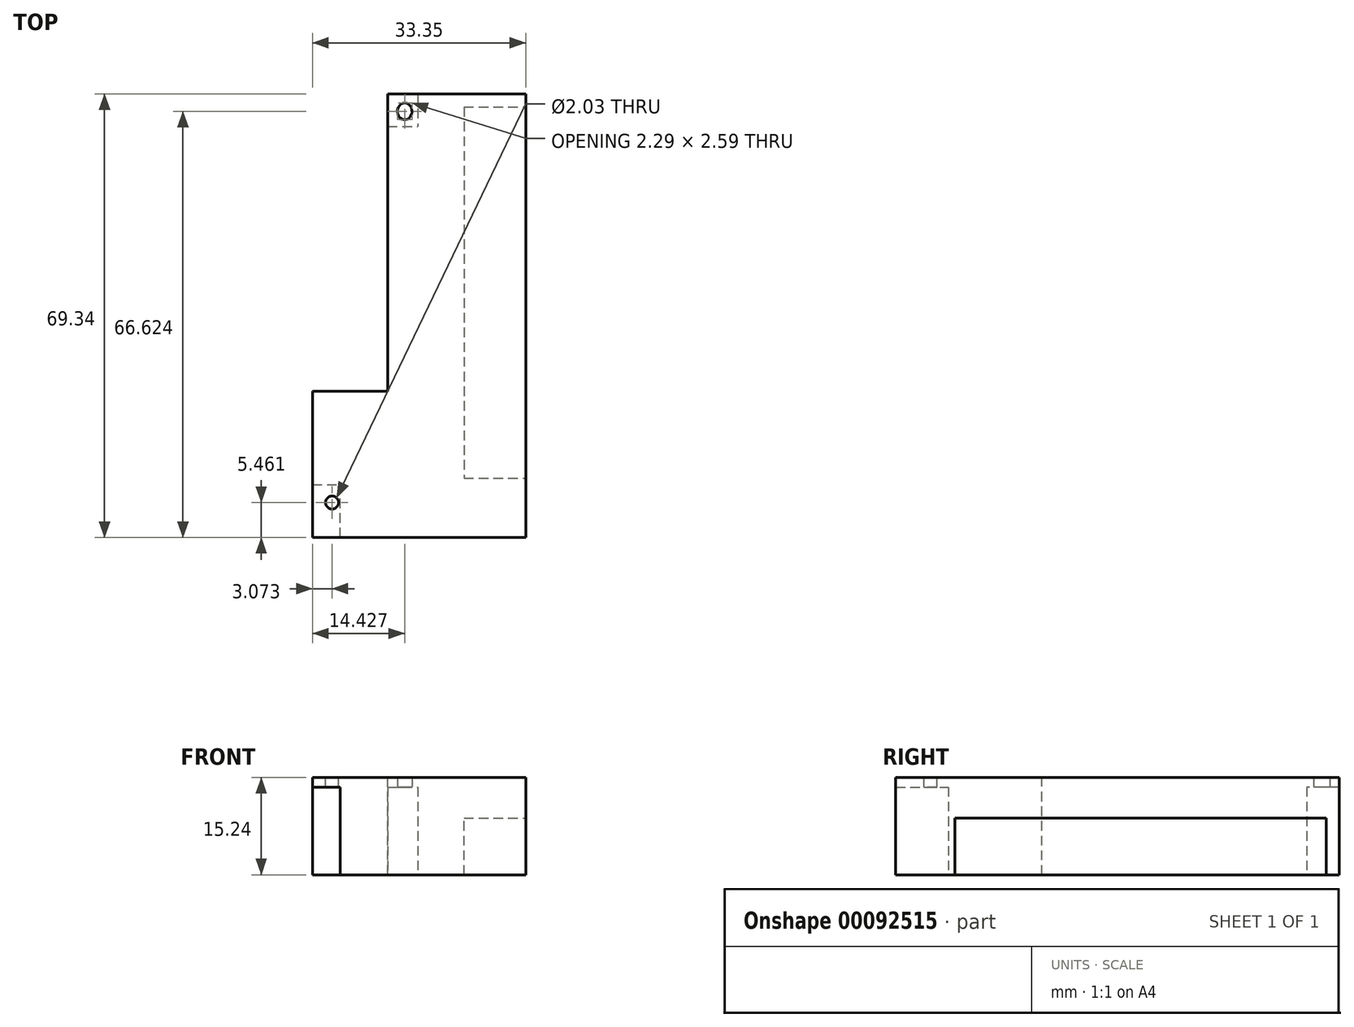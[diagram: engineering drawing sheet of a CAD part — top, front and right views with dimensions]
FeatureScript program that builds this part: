
annotation { "Feature Type Name" : "Feature", "Feature Type Description" : "" }
export const myFeature = defineFeature(function(context is Context, id is Id, definition is map)
    precondition{}
    {
        {
            var Q0;
            Q0=qCreatedBy(makeId("Top.planeOp"),FACE);
            var sketch = newSketch(context, id + "F0", { "sketchPlane" : qUnion([Q0])});
            skLineSegment(sketch, "E0.bottom", {"start": v(-21.6, 69.34) * mm, "end": v(0, 69.34) * mm});
            skLineSegment(sketch, "E0.top", {"start": v(-21.6, 0) * mm, "end": v(0, 0) * mm});
            skLineSegment(sketch, "E0.left", {"start": v(-21.6, 69.34) * mm, "end": v(-21.6, 22.86) * mm});
            skLineSegment(sketch, "E0.right", {"start": v(0, 69.34) * mm, "end": v(0, 0) * mm});
            skLineSegment(sketch, "E1.bottom", {"start": v(-21.6, 0) * mm, "end": v(-33.35, 0) * mm});
            skLineSegment(sketch, "E1.top", {"start": v(-21.6, 22.86) * mm, "end": v(-33.35, 22.86) * mm});
            skLineSegment(sketch, "E1.right", {"start": v(-33.35, 0) * mm, "end": v(-33.35, 22.86) * mm});
            skCircle(sketch, "E2", {"center": v(-30.28, 5.46) * mm, "radius": 1.02 * mm});
            skLineSegment(sketch, "E3", {"start": v(-33.35, 9.14) * mm, "end": v(0, 9.14) * mm});
            skEllipse(sketch, "E4", {"center": v(-18.92, 66.62) * mm, "majorRadius": 1.3 * mm, "minorRadius": 1.14 * mm, "majorAxis": v(0, 1)});
            skSolve(sketch);
        }
        {
            var Q0;
            {var subQ2=sQuery(id+"F0.wireOp",EDGE,"E0.bottom");Q0=makeQuery(id+"F0.imprint","IMPRINT",FACE,{"disambiguationData":[TD([[makeQuery(id+"F0.imprint","IMPRINT",EDGE,{"derivedFrom":subQ2}),-1.0]])]});}
            var Q1;
            {var subQ4=sQuery(id+"F0.wireOp",EDGE,"E0.top");Q1=makeQuery(id+"F0.imprint","IMPRINT",FACE,{"disambiguationData":[TD([[makeQuery(id+"F0.imprint","IMPRINT",EDGE,{"derivedFrom":subQ4}),1.0]])]});}
            extrude(context, id + "F1", {"entities" : qUnion([Q0, Q1]), "oppositeDirection" : true, "depth" : 15.24 * mm});
        }
        {
            var Q0;
            Q0=makeQuery(id+"F1.opExtrude","CAP_FACE",FACE,{"disambiguationData":[OSD([sQuery(id+"F0.wireOp",EDGE,"E0.bottom"),sQuery(id+"F0.wireOp",EDGE,"E0.top"),sQuery(id+"F0.wireOp",EDGE,"E0.left"),sQuery(id+"F0.wireOp",EDGE,"E0.right"),sQuery(id+"F0.wireOp",EDGE,"E1.bottom"),sQuery(id+"F0.wireOp",EDGE,"E1.top"),sQuery(id+"F0.wireOp",EDGE,"E1.right"),sQuery(id+"F0.wireOp",EDGE,"E2"),sQuery(id+"F0.wireOp",EDGE,"E4")])],"isStart":false});
            var sketch = newSketch(context, id + "F2", { "sketchPlane" : qUnion([Q0])});
            skLineSegment(sketch, "E5.bottom", {"start": v(-33.35, 0) * mm, "end": v(-29.03, 0) * mm});
            skLineSegment(sketch, "E5.top", {"start": v(-33.35, -8.26) * mm, "end": v(-29.03, -8.26) * mm});
            skLineSegment(sketch, "E5.left", {"start": v(-33.35, 0) * mm, "end": v(-33.35, -8.26) * mm});
            skLineSegment(sketch, "E5.right", {"start": v(-29.03, 0) * mm, "end": v(-29.03, -8.26) * mm});
            skSolve(sketch);
        }
        {
            var Q0;
            Q0=makeQuery(id+"F2.imprint","IMPRINT",FACE,{"disambiguationData":[TD([[makeQuery(id+"F2.imprint","IMPRINT",EDGE,{"derivedFrom":sQuery(id+"F2.wireOp",EDGE,"E5.bottom")}),1.0]])]});
            extrude(context, id + "F3", {"entities" : qUnion([Q0]), "operationType" : NewBodyOperationType.REMOVE, "oppositeDirection" : true, "depth" : 13.72 * mm});
        }
        {
            var Q0;
            Q0=makeQuery(id+"F1.opExtrude","CAP_FACE",FACE,{"disambiguationData":[OSD([sQuery(id+"F0.wireOp",EDGE,"E0.bottom"),sQuery(id+"F0.wireOp",EDGE,"E0.top"),sQuery(id+"F0.wireOp",EDGE,"E0.left"),sQuery(id+"F0.wireOp",EDGE,"E0.right"),sQuery(id+"F0.wireOp",EDGE,"E1.bottom"),sQuery(id+"F0.wireOp",EDGE,"E1.top"),sQuery(id+"F0.wireOp",EDGE,"E1.right"),sQuery(id+"F0.wireOp",EDGE,"E2"),sQuery(id+"F0.wireOp",EDGE,"E4")])],"isStart":false});
            var sketch = newSketch(context, id + "F4", { "sketchPlane" : qUnion([Q0])});
            skLineSegment(sketch, "E6.bottom", {"start": v(-21.6, -69.34) * mm, "end": v(-16.9, -69.34) * mm});
            skLineSegment(sketch, "E6.top", {"start": v(-21.6, -64.26) * mm, "end": v(-16.9, -64.26) * mm});
            skLineSegment(sketch, "E6.left", {"start": v(-21.6, -69.34) * mm, "end": v(-21.6, -64.26) * mm});
            skLineSegment(sketch, "E6.right", {"start": v(-16.9, -69.34) * mm, "end": v(-16.9, -64.26) * mm});
            skSolve(sketch);
        }
        {
            var Q0;
            Q0 = qSketchRegion(id + "F4", true);
            extrude(context, id + "F5", {"entities" : qUnion([Q0]), "operationType" : NewBodyOperationType.REMOVE, "oppositeDirection" : true, "depth" : 13.72 * mm});
        }
        {
            var Q0;
            Q0=makeQuery(id+"F1.opExtrude","SWEPT_FACE",FACE,{"disambiguationData":[OSD([sQuery(id+"F0.wireOp",EDGE,"E0.right")])]});
            var sketch = newSketch(context, id + "F6", { "sketchPlane" : qUnion([Q0])});
            skLineSegment(sketch, "E7.bottom", {"start": v(9.27, -15.24) * mm, "end": v(67.3, -15.24) * mm});
            skLineSegment(sketch, "E7.top", {"start": v(9.27, -6.35) * mm, "end": v(67.3, -6.35) * mm});
            skLineSegment(sketch, "E7.left", {"start": v(9.27, -15.24) * mm, "end": v(9.27, -6.35) * mm});
            skLineSegment(sketch, "E7.right", {"start": v(67.3, -15.24) * mm, "end": v(67.3, -6.35) * mm});
            skSolve(sketch);
        }
        {
            var Q0;
            Q0=makeQuery(id+"F6.imprint","IMPRINT",FACE,{"disambiguationData":[TD([[makeQuery(id+"F6.imprint","IMPRINT",EDGE,{"derivedFrom":sQuery(id+"F6.wireOp",EDGE,"E7.bottom")}),-1.0]])]});
            extrude(context, id + "F7", {"entities" : qUnion([Q0]), "operationType" : NewBodyOperationType.REMOVE, "oppositeDirection" : true, "depth" : 9.65 * mm});
        }
    });
